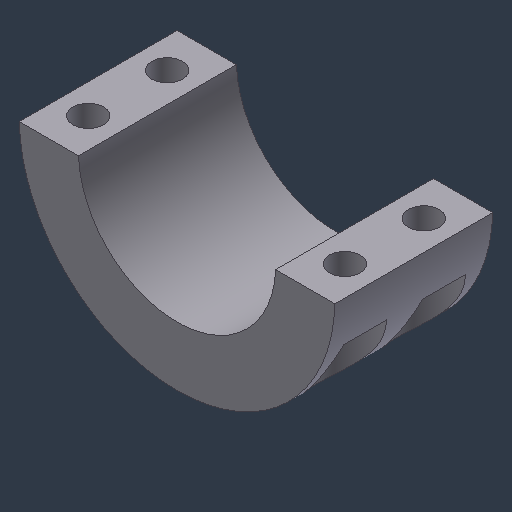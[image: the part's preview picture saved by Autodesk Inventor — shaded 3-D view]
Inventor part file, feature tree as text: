
AUTODESK INVENTOR PART (.ipt)
format: ipt  version: 2024.3 (Build 283343000, 343)  size: 139,264 bytes
history: native  units: mm (DEFAULTED — no unit token found)
features: sketch x3, hole x2, extrude x1, plane x1
ambient origin geometry x8: Origin, YZ Plane, XZ Plane, XY Plane, X Axis, Y Axis, Z Axis, Center Point
bodies: Solid1 (feature_tree)
feature tree (7):
  extrude  "Extrusion1"  Depth=0.635mm
  hole  "Hole1"  [1 undecoded]
  plane  "Work Plane1"
  hole  "Hole2"  [1 undecoded]
  sketch  "Sketch2"  dims[d0=25.4mm d1=0.635mm]
  sketch  "Sketch3"  dims[d3=25.4mm d4=0.0mm]
  sketch  "Sketch4"  dims[d5=31.75mm d6=19.05mm d7=9.525mm d8=6.35mm d9=14.3117mm d10=25.4mm d11=20.594885mm d12=-12.7mm d13=41.275mm d14=12.7mm d15=4.9784mm d16=9.652mm d17=9.525mm d18=4.826mm d19=14.3117mm d20=13.6144mm d21=20.594885mm]
note: 2 required parameter values undecoded (feature->parameter linkage not recoverable at this tier; creation-order binding heuristic only, values carry confidence <= 0.55)
